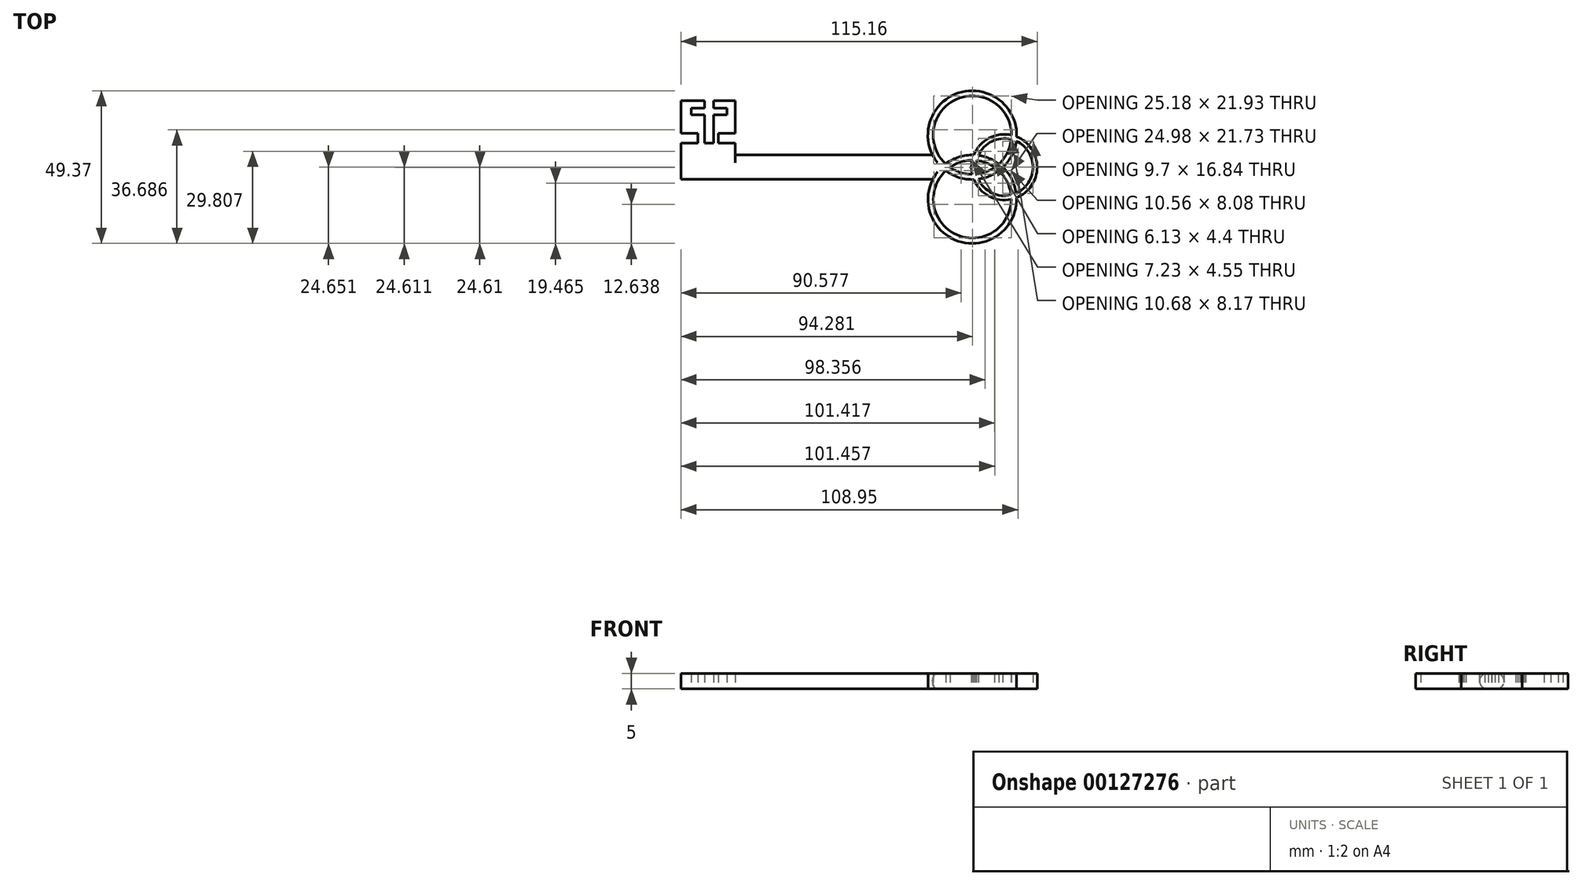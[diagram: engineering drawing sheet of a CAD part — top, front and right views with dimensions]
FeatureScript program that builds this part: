
annotation { "Feature Type Name" : "Feature", "Feature Type Description" : "" }
export const myFeature = defineFeature(function(context is Context, id is Id, definition is map)
    precondition{}
    {
        {
            var Q0;
            Q0=qCreatedBy(makeId("Top.planeOp"),FACE);
            var sketch = newSketch(context, id + "F0", { "sketchPlane" : qUnion([Q0])});
            skCircle(sketch, "E0", {"center": v(53.01, 9.25) * mm, "radius": 14.35 * mm});
            skCircle(sketch, "E1", {"center": v(53.01, -11.47) * mm, "radius": 14.3 * mm});
            skCircle(sketch, "E2", {"center": v(63.37, -1.1) * mm, "radius": 10.61 * mm});
            skLineSegment(sketch, "E3.right", {"start": v(-41.18, 2.84) * mm, "end": v(-41.18, -5.05) * mm});
            skLineSegment(sketch, "E4.top", {"start": v(-41.18, 20.34) * mm, "end": v(-23.67, 20.34) * mm});
            skLineSegment(sketch, "E4.left", {"start": v(-41.18, 2.84) * mm, "end": v(-41.18, 20.34) * mm});
            skLineSegment(sketch, "E4.right", {"start": v(-23.67, 2.84) * mm, "end": v(-23.67, 20.34) * mm});
            skLineSegment(sketch, "E5", {"start": v(-23.67, 2.84) * mm, "end": v(40.17, 2.84) * mm});
            skLineSegment(sketch, "E6.trimOffspring", {"start": v(40.22, -5.05) * mm, "end": v(-41.18, -5.05) * mm});
            skCircle(sketch, "E7", {"center": v(53.01, 9.25) * mm, "radius": 12.68 * mm});
            skCircle(sketch, "E8", {"center": v(63.37, -1.1) * mm, "radius": 9.25 * mm});
            skCircle(sketch, "E9", {"center": v(53.01, -11.47) * mm, "radius": 12.58 * mm});
            skSolve(sketch);
        }
        {
            var Q0;
            Q0=makeQuery(id+"F0.imprint","IMPRINT",FACE,{"disambiguationData":[TD([[makeQuery(id+"F0.imprint","IMPRINT",EDGE,{"derivedFrom":sQuery(id+"F0.wireOp",EDGE,"E3.right")}),1.0]])]});
            var Q1;
            {var subQ1=sQuery(id+"F0.wireOp",EDGE,"E0");var subQ5=makeQuery(id+"F0.imprint","INTERSECT",VERTEX,{"derivedFrom":[subQ1,sQuery(id+"F0.wireOp",EDGE,"E5")]});Q1=makeQuery(id+"F0.imprint","IMPRINT",FACE,{"disambiguationData":[TD([[makeQuery(id+"F0.imprint","IMPRINT",EDGE,{"disambiguationData":[TD([[subQ5,-1.0]])],"derivedFrom":subQ1}),1.0]])]});}
            var Q2;
            {var subQ1=sQuery(id+"F0.wireOp",EDGE,"E1");var subQ6=sQuery(id+"F0.wireOp",EDGE,"E0");var subQ7=makeQuery(id+"F0.imprint","INTERSECT",VERTEX,{"disambiguationData":[OD(0.0)],"derivedFrom":[subQ6,subQ1]});Q2=makeQuery(id+"F0.imprint","IMPRINT",FACE,{"disambiguationData":[TD([[makeQuery(id+"F0.imprint","IMPRINT",EDGE,{"disambiguationData":[TD([[subQ7,-1.0]])],"derivedFrom":subQ6}),-1.0]])]});}
            var Q3;
            {var subQ0=sQuery(id+"F0.wireOp",EDGE,"E2");var subQ1=sQuery(id+"F0.wireOp",EDGE,"E0");var subQ2=makeQuery(id+"F0.imprint","INTERSECT",VERTEX,{"disambiguationData":[OD(0.0)],"derivedFrom":[subQ1,subQ0]});Q3=makeQuery(id+"F0.imprint","IMPRINT",FACE,{"disambiguationData":[TD([[makeQuery(id+"F0.imprint","IMPRINT",EDGE,{"disambiguationData":[TD([[subQ2,1.0]])],"derivedFrom":subQ1}),-1.0]])]});}
            var Q4;
            {var subQ0=sQuery(id+"F0.wireOp",EDGE,"E2");var subQ1=sQuery(id+"F0.wireOp",EDGE,"E0");var subQ2=makeQuery(id+"F0.imprint","INTERSECT",VERTEX,{"disambiguationData":[OD(1.0)],"derivedFrom":[subQ1,subQ0]});Q4=makeQuery(id+"F0.imprint","IMPRINT",FACE,{"disambiguationData":[TD([[makeQuery(id+"F0.imprint","IMPRINT",EDGE,{"disambiguationData":[TD([[subQ2,-1.0]])],"derivedFrom":subQ1}),-1.0]])]});}
            var Q5;
            {var subQ0=sQuery(id+"F0.wireOp",EDGE,"E9");var subQ1=sQuery(id+"F0.wireOp",EDGE,"E2");var subQ2=makeQuery(id+"F0.imprint","INTERSECT",VERTEX,{"disambiguationData":[OD(0.0)],"derivedFrom":[subQ1,subQ0]});Q5=makeQuery(id+"F0.imprint","IMPRINT",FACE,{"disambiguationData":[TD([[makeQuery(id+"F0.imprint","IMPRINT",EDGE,{"disambiguationData":[TD([[subQ2,-1.0]])],"derivedFrom":subQ1}),1.0]])]});}
            var Q6;
            {var subQ0=sQuery(id+"F0.wireOp",EDGE,"E8");var subQ1=sQuery(id+"F0.wireOp",EDGE,"E1");var subQ2=makeQuery(id+"F0.imprint","INTERSECT",VERTEX,{"disambiguationData":[OD(1.0)],"derivedFrom":[subQ1,subQ0]});Q6=makeQuery(id+"F0.imprint","IMPRINT",FACE,{"disambiguationData":[TD([[makeQuery(id+"F0.imprint","IMPRINT",EDGE,{"disambiguationData":[TD([[subQ2,-1.0]])],"derivedFrom":subQ1}),-1.0]])]});}
            var Q7;
            {var subQ0=sQuery(id+"F0.wireOp",EDGE,"E7");var subQ1=sQuery(id+"F0.wireOp",EDGE,"E1");var subQ2=makeQuery(id+"F0.imprint","INTERSECT",VERTEX,{"disambiguationData":[OD(0.0)],"derivedFrom":[subQ1,subQ0]});Q7=makeQuery(id+"F0.imprint","IMPRINT",FACE,{"disambiguationData":[TD([[makeQuery(id+"F0.imprint","IMPRINT",EDGE,{"disambiguationData":[TD([[subQ2,-1.0]])],"derivedFrom":subQ1}),1.0]])]});}
            var Q8;
            {var subQ0=sQuery(id+"F0.wireOp",EDGE,"E2");var subQ1=sQuery(id+"F0.wireOp",EDGE,"E1");var subQ2=makeQuery(id+"F0.imprint","INTERSECT",VERTEX,{"disambiguationData":[OD(1.0)],"derivedFrom":[subQ1,subQ0]});Q8=makeQuery(id+"F0.imprint","IMPRINT",FACE,{"disambiguationData":[TD([[makeQuery(id+"F0.imprint","IMPRINT",EDGE,{"disambiguationData":[TD([[subQ2,-1.0]])],"derivedFrom":subQ1}),1.0]])]});}
            var Q9;
            {var subQ0=sQuery(id+"F0.wireOp",EDGE,"E1");var subQ1=sQuery(id+"F0.wireOp",EDGE,"E0");var subQ2=makeQuery(id+"F0.imprint","INTERSECT",VERTEX,{"disambiguationData":[OD(0.0)],"derivedFrom":[subQ1,subQ0]});Q9=makeQuery(id+"F0.imprint","IMPRINT",FACE,{"disambiguationData":[TD([[makeQuery(id+"F0.imprint","IMPRINT",EDGE,{"disambiguationData":[TD([[subQ2,-1.0]])],"derivedFrom":subQ1}),1.0]])]});}
            var Q10;
            {var subQ0=sQuery(id+"F0.wireOp",EDGE,"E9");var subQ1=sQuery(id+"F0.wireOp",EDGE,"E0");var subQ2=makeQuery(id+"F0.imprint","INTERSECT",VERTEX,{"disambiguationData":[OD(0.0)],"derivedFrom":[subQ1,subQ0]});Q10=makeQuery(id+"F0.imprint","IMPRINT",FACE,{"disambiguationData":[TD([[makeQuery(id+"F0.imprint","IMPRINT",EDGE,{"disambiguationData":[TD([[subQ2,-1.0]])],"derivedFrom":subQ1}),1.0]])]});}
            var Q11;
            {var subQ0=sQuery(id+"F0.wireOp",EDGE,"E2");var subQ1=sQuery(id+"F0.wireOp",EDGE,"E0");var subQ2=makeQuery(id+"F0.imprint","INTERSECT",VERTEX,{"disambiguationData":[OD(1.0)],"derivedFrom":[subQ1,subQ0]});Q11=makeQuery(id+"F0.imprint","IMPRINT",FACE,{"disambiguationData":[TD([[makeQuery(id+"F0.imprint","IMPRINT",EDGE,{"disambiguationData":[TD([[subQ2,-1.0]])],"derivedFrom":subQ1}),1.0]])]});}
            var Q12;
            {var subQ0=sQuery(id+"F0.wireOp",EDGE,"E8");var subQ1=sQuery(id+"F0.wireOp",EDGE,"E1");var subQ2=makeQuery(id+"F0.imprint","INTERSECT",VERTEX,{"disambiguationData":[OD(1.0)],"derivedFrom":[subQ1,subQ0]});Q12=makeQuery(id+"F0.imprint","IMPRINT",FACE,{"disambiguationData":[TD([[makeQuery(id+"F0.imprint","IMPRINT",EDGE,{"disambiguationData":[TD([[subQ2,-1.0]])],"derivedFrom":subQ1}),1.0]])]});}
            var Q13;
            {var subQ0=sQuery(id+"F0.wireOp",EDGE,"E8");var subQ1=sQuery(id+"F0.wireOp",EDGE,"E0");var subQ2=makeQuery(id+"F0.imprint","INTERSECT",VERTEX,{"disambiguationData":[OD(0.0)],"derivedFrom":[subQ1,subQ0]});Q13=makeQuery(id+"F0.imprint","IMPRINT",FACE,{"disambiguationData":[TD([[makeQuery(id+"F0.imprint","IMPRINT",EDGE,{"disambiguationData":[TD([[subQ2,-1.0]])],"derivedFrom":subQ1}),1.0]])]});}
            var Q14;
            {var subQ0=sQuery(id+"F0.wireOp",EDGE,"E9");var subQ1=sQuery(id+"F0.wireOp",EDGE,"E0");var subQ2=makeQuery(id+"F0.imprint","INTERSECT",VERTEX,{"disambiguationData":[OD(1.0)],"derivedFrom":[subQ1,subQ0]});Q14=makeQuery(id+"F0.imprint","IMPRINT",FACE,{"disambiguationData":[TD([[makeQuery(id+"F0.imprint","IMPRINT",EDGE,{"disambiguationData":[TD([[subQ2,-1.0]])],"derivedFrom":subQ1}),1.0]])]});}
            var Q15;
            {var subQ0=sQuery(id+"F0.wireOp",EDGE,"E1");var subQ1=sQuery(id+"F0.wireOp",EDGE,"E0");var subQ2=makeQuery(id+"F0.imprint","INTERSECT",VERTEX,{"disambiguationData":[OD(1.0)],"derivedFrom":[subQ1,subQ0]});Q15=makeQuery(id+"F0.imprint","IMPRINT",FACE,{"disambiguationData":[TD([[makeQuery(id+"F0.imprint","IMPRINT",EDGE,{"disambiguationData":[TD([[subQ2,-1.0]])],"derivedFrom":subQ1}),1.0]])]});}
            var Q16;
            {var subQ0=sQuery(id+"F0.wireOp",EDGE,"E2");var subQ1=sQuery(id+"F0.wireOp",EDGE,"E0");var subQ2=makeQuery(id+"F0.imprint","INTERSECT",VERTEX,{"disambiguationData":[OD(0.0)],"derivedFrom":[subQ1,subQ0]});Q16=makeQuery(id+"F0.imprint","IMPRINT",FACE,{"disambiguationData":[TD([[makeQuery(id+"F0.imprint","IMPRINT",EDGE,{"disambiguationData":[TD([[subQ2,1.0]])],"derivedFrom":subQ1}),1.0]])]});}
            var Q17;
            {var subQ0=sQuery(id+"F0.wireOp",EDGE,"E9");var subQ1=sQuery(id+"F0.wireOp",EDGE,"E0");var subQ2=makeQuery(id+"F0.imprint","INTERSECT",VERTEX,{"disambiguationData":[OD(1.0)],"derivedFrom":[subQ1,subQ0]});Q17=makeQuery(id+"F0.imprint","IMPRINT",FACE,{"disambiguationData":[TD([[makeQuery(id+"F0.imprint","IMPRINT",EDGE,{"disambiguationData":[TD([[subQ2,-1.0]])],"derivedFrom":subQ1}),-1.0]])]});}
            var Q18;
            {var subQ0=sQuery(id+"F0.wireOp",EDGE,"E2");var subQ1=sQuery(id+"F0.wireOp",EDGE,"E1");var subQ2=makeQuery(id+"F0.imprint","INTERSECT",VERTEX,{"disambiguationData":[OD(0.0)],"derivedFrom":[subQ1,subQ0]});Q18=makeQuery(id+"F0.imprint","IMPRINT",FACE,{"disambiguationData":[TD([[makeQuery(id+"F0.imprint","IMPRINT",EDGE,{"disambiguationData":[TD([[subQ2,-1.0]])],"derivedFrom":subQ1}),1.0]])]});}
            extrude(context, id + "F1", {"entities" : qUnion([Q0, Q1, Q2, Q3, Q4, Q5, Q6, Q7, Q8, Q9, Q10, Q11, Q12, Q13, Q14, Q15, Q16, Q17, Q18]), "depth" : 5 * mm});
        }
        {
            var Q0;
            Q0=makeQuery(id+"F1.opExtrude","CAP_EDGE",EDGE,{"disambiguationData":[OSD([sQuery(id+"F0.wireOp",EDGE,"E6.trimOffspring")])],"isStart":false});
            var Q1;
            Q1=makeQuery(id+"F1.opExtrude","CAP_EDGE",EDGE,{"disambiguationData":[OSD([sQuery(id+"F0.wireOp",EDGE,"E6.trimOffspring")])],"isStart":true});
            var Q2;
            Q2=makeQuery(id+"F1.opExtrude","CAP_EDGE",EDGE,{"disambiguationData":[OSD([sQuery(id+"F0.wireOp",EDGE,"E5")])],"isStart":false});
            var Q3;
            Q3=makeQuery(id+"F1.opExtrude","CAP_EDGE",EDGE,{"disambiguationData":[OSD([sQuery(id+"F0.wireOp",EDGE,"E5")])],"isStart":true});
            fillet(context, id + "F2", {"entities" : qUnion([Q0, Q1, Q2, Q3]), "radius" : 2.5 * mm, "tangentPropagation" : true, "allowEdgeOverflow" : false});
        }
        {
            var Q0;
            Q0=makeQuery(id+"F1.opExtrude","CAP_FACE",FACE,{"disambiguationData":[OSD([sQuery(id+"F0.wireOp",EDGE,"E0"),sQuery(id+"F0.wireOp",EDGE,"E1"),sQuery(id+"F0.wireOp",EDGE,"E2"),sQuery(id+"F0.wireOp",EDGE,"E3.right"),sQuery(id+"F0.wireOp",EDGE,"E4.top"),sQuery(id+"F0.wireOp",EDGE,"E4.left"),sQuery(id+"F0.wireOp",EDGE,"E4.right"),sQuery(id+"F0.wireOp",EDGE,"E5"),sQuery(id+"F0.wireOp",EDGE,"E6.trimOffspring"),sQuery(id+"F0.wireOp",EDGE,"E7"),sQuery(id+"F0.wireOp",EDGE,"E8"),sQuery(id+"F0.wireOp",EDGE,"E9")])],"isStart":true});
            var sketch = newSketch(context, id + "F3", { "sketchPlane" : qUnion([Q0])});
            skLineSegment(sketch, "E10.bottom", {"start": v(-23.67, -6.65) * mm, "end": v(-29.15, -6.65) * mm});
            skLineSegment(sketch, "E10.top", {"start": v(-23.67, -9.78) * mm, "end": v(-29.15, -9.78) * mm});
            skLineSegment(sketch, "E10.left", {"start": v(-23.67, -6.65) * mm, "end": v(-23.67, -9.78) * mm});
            skLineSegment(sketch, "E10.right", {"start": v(-29.15, -6.65) * mm, "end": v(-29.15, -9.78) * mm});
            skLineSegment(sketch, "E11.bottom", {"start": v(-41.18, -6.65) * mm, "end": v(-35.7, -6.65) * mm});
            skLineSegment(sketch, "E11.top", {"start": v(-41.18, -9.78) * mm, "end": v(-35.7, -9.78) * mm});
            skLineSegment(sketch, "E11.left", {"start": v(-41.18, -6.65) * mm, "end": v(-41.18, -9.78) * mm});
            skLineSegment(sketch, "E11.right", {"start": v(-35.7, -6.65) * mm, "end": v(-35.7, -9.78) * mm});
            skLineSegment(sketch, "E12.bottom", {"start": v(-33.51, -6.65) * mm, "end": v(-30.65, -6.65) * mm});
            skLineSegment(sketch, "E12.top", {"start": v(-33.51, -20.34) * mm, "end": v(-30.65, -20.34) * mm});
            skLineSegment(sketch, "E12.left", {"start": v(-33.51, -6.65) * mm, "end": v(-33.51, -20.34) * mm});
            skLineSegment(sketch, "E12.right", {"start": v(-30.65, -6.65) * mm, "end": v(-30.65, -20.34) * mm});
            skLineSegment(sketch, "E13.bottom", {"start": v(-37.87, -15.77) * mm, "end": v(-26.3, -15.77) * mm});
            skLineSegment(sketch, "E13.top", {"start": v(-37.87, -17.95) * mm, "end": v(-26.3, -17.95) * mm});
            skLineSegment(sketch, "E13.left", {"start": v(-37.87, -15.77) * mm, "end": v(-37.87, -17.95) * mm});
            skLineSegment(sketch, "E13.right", {"start": v(-26.3, -15.77) * mm, "end": v(-26.3, -17.95) * mm});
            skSolve(sketch);
        }
        {
            var Q0;
            Q0=makeQuery(id+"F3.imprint","IMPRINT",FACE,{"disambiguationData":[TD([[makeQuery(id+"F3.imprint","IMPRINT",EDGE,{"derivedFrom":sQuery(id+"F3.wireOp",EDGE,"E11.bottom")}),-1.0]])]});
            var Q1;
            Q1=makeQuery(id+"F3.imprint","IMPRINT",FACE,{"disambiguationData":[TD([[makeQuery(id+"F3.imprint","IMPRINT",EDGE,{"derivedFrom":sQuery(id+"F3.wireOp",EDGE,"E10.bottom")}),1.0]])]});
            var Q2;
            {var subQ0=sQuery(id+"F3.wireOp",EDGE,"E12.bottom");Q2=makeQuery(id+"F3.imprint","IMPRINT",FACE,{"disambiguationData":[TD([[makeQuery(id+"F3.imprint","IMPRINT",EDGE,{"derivedFrom":subQ0}),-1.0]])]});}
            var Q3;
            {var subQ0=sQuery(id+"F3.wireOp",EDGE,"E13.bottom");var subQ1=sQuery(id+"F3.wireOp",EDGE,"E12.left");var subQ2=makeQuery(id+"F3.imprint","INTERSECT",VERTEX,{"derivedFrom":[subQ1,subQ0]});Q3=makeQuery(id+"F3.imprint","IMPRINT",FACE,{"disambiguationData":[TD([[makeQuery(id+"F3.imprint","IMPRINT",EDGE,{"disambiguationData":[TD([[subQ2,-1.0]])],"derivedFrom":subQ1}),1.0]])]});}
            var Q4;
            {var subQ0=sQuery(id+"F3.wireOp",EDGE,"E12.top");Q4=makeQuery(id+"F3.imprint","IMPRINT",FACE,{"disambiguationData":[TD([[makeQuery(id+"F3.imprint","IMPRINT",EDGE,{"derivedFrom":subQ0}),1.0]])]});}
            var Q5;
            {var subQ5=sQuery(id+"F3.wireOp",EDGE,"E13.right");Q5=makeQuery(id+"F3.imprint","IMPRINT",FACE,{"disambiguationData":[TD([[makeQuery(id+"F3.imprint","IMPRINT",EDGE,{"derivedFrom":subQ5}),-1.0]])]});}
            var Q6;
            {var subQ5=sQuery(id+"F3.wireOp",EDGE,"E13.left");Q6=makeQuery(id+"F3.imprint","IMPRINT",FACE,{"disambiguationData":[TD([[makeQuery(id+"F3.imprint","IMPRINT",EDGE,{"derivedFrom":subQ5}),1.0]])]});}
            extrude(context, id + "F4", {"entities" : qUnion([Q0, Q1, Q2, Q3, Q4, Q5, Q6]), "operationType" : NewBodyOperationType.REMOVE, "oppositeDirection" : true, "depth" : 25 * mm});
        }
    });
